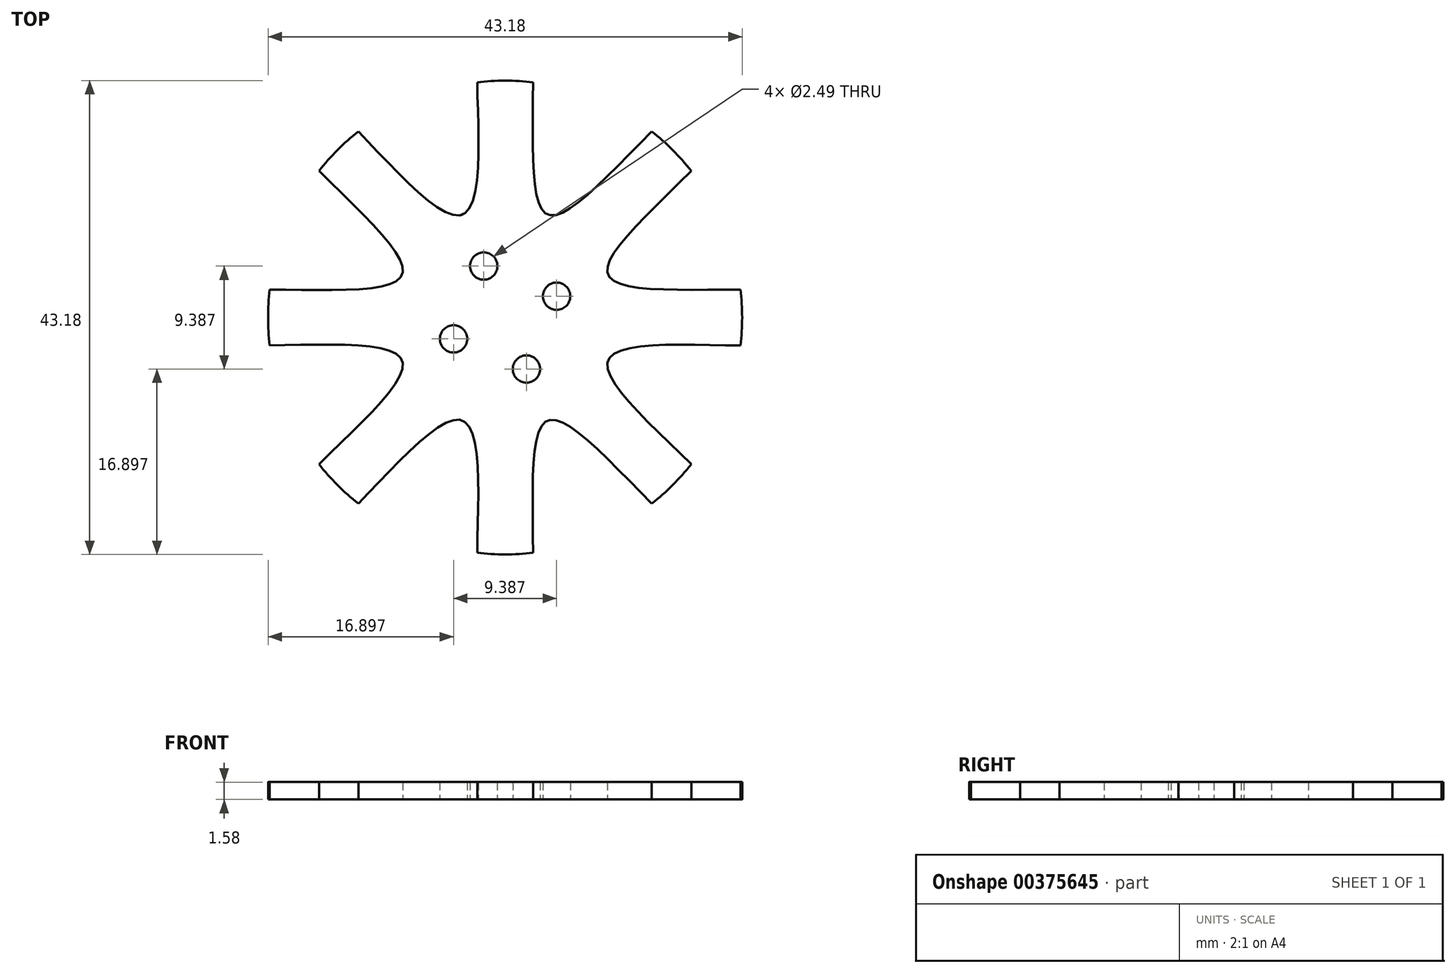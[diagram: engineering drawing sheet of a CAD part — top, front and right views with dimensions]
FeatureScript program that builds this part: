
annotation { "Feature Type Name" : "Feature", "Feature Type Description" : "" }
export const myFeature = defineFeature(function(context is Context, id is Id, definition is map)
    precondition{}
    {
        {
            var Q0;
            Q0=qCreatedBy(makeId("Top.planeOp"),FACE);
            var sketch = newSketch(context, id + "F0", { "sketchPlane" : qUnion([Q0])});
            skLineSegment(sketch, "E0", {"start": v(0, 30.67) * mm, "end": v(0, -28.01) * mm, "construction": true});
            skLineSegment(sketch, "E1", {"start": v(-28.25, 0) * mm, "end": v(29.1, 0) * mm, "construction": true});
            skLineSegment(sketch, "E2", {"start": v(-21.4, 21.4) * mm, "end": v(20.62, -20.62) * mm, "construction": true});
            skLineSegment(sketch, "E3", {"start": v(21.66, 21.66) * mm, "end": v(-18.96, -18.96) * mm, "construction": true});
            skArc(sketch, "E4", {"start": v(-16.96, 13.36) * mm, "mid": v(-15.27, 15.27) * mm, "end": v(-13.36, 16.96) * mm});
            skArc(sketch, "E5", {"start": v(-2.54, 21.44) * mm, "mid": v(0, 21.59) * mm, "end": v(2.54, 21.44) * mm});
            skArc(sketch, "E6", {"start": v(13.36, 16.96) * mm, "mid": v(15.27, 15.27) * mm, "end": v(16.96, 13.36) * mm});
            skArc(sketch, "E7", {"start": v(-13.36, 16.96) * mm, "mid": v(-6.9, 16.66) * mm, "end": v(-2.54, 21.44) * mm});
            skArc(sketch, "E8", {"start": v(2.54, 21.44) * mm, "mid": v(6.9, 16.66) * mm, "end": v(13.36, 16.96) * mm});
            skArc(sketch, "E9", {"start": v(21.44, 2.54) * mm, "mid": v(21.6, 0) * mm, "end": v(21.44, -2.54) * mm});
            skArc(sketch, "E10", {"start": v(16.96, -13.36) * mm, "mid": v(15.27, -15.27) * mm, "end": v(13.36, -16.96) * mm});
            skArc(sketch, "E11", {"start": v(2.54, -21.44) * mm, "mid": v(0, -21.6) * mm, "end": v(-2.54, -21.44) * mm});
            skArc(sketch, "E12", {"start": v(-13.36, -16.96) * mm, "mid": v(-15.27, -15.27) * mm, "end": v(-16.96, -13.36) * mm});
            skArc(sketch, "E13", {"start": v(-21.44, -2.54) * mm, "mid": v(-21.59, 0) * mm, "end": v(-21.44, 2.54) * mm});
            skArc(sketch, "E14", {"start": v(-21.44, 2.54) * mm, "mid": v(-16.66, 6.9) * mm, "end": v(-16.96, 13.36) * mm});
            skArc(sketch, "E15", {"start": v(-16.96, -13.36) * mm, "mid": v(-16.66, -6.9) * mm, "end": v(-21.44, -2.54) * mm});
            skArc(sketch, "E16", {"start": v(-2.54, -21.44) * mm, "mid": v(-6.9, -16.66) * mm, "end": v(-13.36, -16.96) * mm});
            skArc(sketch, "E17", {"start": v(13.36, -16.96) * mm, "mid": v(6.9, -16.66) * mm, "end": v(2.54, -21.44) * mm});
            skArc(sketch, "E18", {"start": v(21.44, -2.54) * mm, "mid": v(16.66, -6.9) * mm, "end": v(16.96, -13.36) * mm});
            skArc(sketch, "E19", {"start": v(16.96, 13.36) * mm, "mid": v(16.66, 6.9) * mm, "end": v(21.44, 2.54) * mm});
            skCircle(sketch, "E20", {"center": v(0, 0) * mm, "radius": 5.08 * mm, "construction": true});
            skCircle(sketch, "E21", {"center": v(4.7, 1.94) * mm, "radius": 1.24 * mm});
            skCircle(sketch, "E22", {"center": v(-4.7, -1.94) * mm, "radius": 1.24 * mm});
            skCircle(sketch, "E23", {"center": v(1.94, -4.7) * mm, "radius": 1.24 * mm});
            skLineSegment(sketch, "E24", {"start": v(-2.42, 5.85) * mm, "end": v(2.68, -6.46) * mm, "construction": true});
            skLineSegment(sketch, "E25", {"start": v(6.63, 2.74) * mm, "end": v(-6.69, -2.77) * mm, "construction": true});
            skCircle(sketch, "E26", {"center": v(-1.94, 4.7) * mm, "radius": 1.24 * mm});
            skSolve(sketch);
        }
        {
            var Q0;
            Q0 = qSketchRegion(id + "F0", true);
            extrude(context, id + "F1", {"entities" : qUnion([Q0]), "endBound" : BoundingType.SYMMETRIC, "depth" : 1.59 * mm});
        }
        {
            var Q0;
            Q0=qCreatedBy(makeId("Front.planeOp"),FACE);
            var sketch = newSketch(context, id + "F2", { "sketchPlane" : qUnion([Q0])});
            skLineSegment(sketch, "E27", {"start": v(0, 9.03) * mm, "end": v(0, -9.77) * mm, "construction": true});
            skSolve(sketch);
        }
        {
            var Q0;
            Q0=makeQuery(id+"F1.opExtrude","CAP_EDGE",EDGE,{"disambiguationData":[OSD([sQuery(id+"F0.wireOp",EDGE,"E6")])],"isStart":false});
            cPoint(context, id + "F3", {"entities" : qUnion([Q0]), "parameter" : 0.5});
        }
        {
            var Q0;
            Q0=makeQuery(id+"F1.opExtrude","CAP_EDGE",EDGE,{"disambiguationData":[OSD([sQuery(id+"F0.wireOp",EDGE,"E6")])],"isStart":false});
            var Q1;
            Q1 = qCreatedBy(id + "F3" ,VERTEX);
            cPlane(context, id + "F4", {"entities" : qUnion([Q0, Q1]), "cplaneType" : CPlaneType.CURVE_POINT, "offset" : 25.4 * mm, "width" : 152.4 * mm, "height" : 152.4 * mm});
        }
        {
            var Q0;
            Q0=makeQuery(id+"F1.opExtrude","CAP_FACE",FACE,{"disambiguationData":[OSD([sQuery(id+"F0.wireOp",EDGE,"E4"),sQuery(id+"F0.wireOp",EDGE,"E5"),sQuery(id+"F0.wireOp",EDGE,"E6"),sQuery(id+"F0.wireOp",EDGE,"E7"),sQuery(id+"F0.wireOp",EDGE,"E8"),sQuery(id+"F0.wireOp",EDGE,"E9"),sQuery(id+"F0.wireOp",EDGE,"E10"),sQuery(id+"F0.wireOp",EDGE,"E11"),sQuery(id+"F0.wireOp",EDGE,"E12"),sQuery(id+"F0.wireOp",EDGE,"E13"),sQuery(id+"F0.wireOp",EDGE,"E14"),sQuery(id+"F0.wireOp",EDGE,"E15"),sQuery(id+"F0.wireOp",EDGE,"E16"),sQuery(id+"F0.wireOp",EDGE,"E17"),sQuery(id+"F0.wireOp",EDGE,"E18"),sQuery(id+"F0.wireOp",EDGE,"E19"),sQuery(id+"F0.wireOp",EDGE,"E21"),sQuery(id+"F0.wireOp",EDGE,"E22"),sQuery(id+"F0.wireOp",EDGE,"E23"),sQuery(id+"F0.wireOp",EDGE,"E26")])],"isStart":false});
            var sketch = newSketch(context, id + "F5", { "sketchPlane" : qUnion([Q0])});
            skLineSegment(sketch, "E28", {"start": v(-19.28, -7.99) * mm, "end": v(21.9, 9.07) * mm, "construction": true});
            skFitSpline(sketch, "E29", {"points": [v(16.96, 13.36) * mm, v(9.39, 3.89) * mm, v(21.44, 2.54) * mm], "startDerivative": vector(-25.12, -25.19) * mm, "endDerivative": vector(34.63, -0.1) * mm});
            skLineSegment(sketch, "E30", {"start": v(-9.53, 23.02) * mm, "end": v(9.33, -22.54) * mm, "construction": true});
            skFitSpline(sketch, "E31", {"points": [v(2.54, -21.44) * mm, v(3.89, -9.39) * mm, v(13.36, -16.96) * mm], "startDerivative": vector(-0.02, 34.1) * mm, "endDerivative": vector(24.11, -24.05) * mm});
            skLineSegment(sketch, "E32", {"start": v(-21.4, 8.86) * mm, "end": v(22.41, -9.28) * mm, "construction": true});
            skLineSegment(sketch, "E33", {"start": v(8.34, 20.12) * mm, "end": v(-8.56, -20.68) * mm, "construction": true});
            skFitSpline(sketch, "E34", {"points": [v(21.44, -2.54) * mm, v(9.39, -3.89) * mm, v(16.96, -13.36) * mm], "startDerivative": vector(-31.53, 0.26) * mm, "endDerivative": vector(22.55, -22.16) * mm});
            skFitSpline(sketch, "E35", {"points": [v(-13.36, -16.96) * mm, v(-3.89, -9.39) * mm, v(-2.54, -21.44) * mm], "startDerivative": vector(20.74, 21.37) * mm, "endDerivative": vector(-0.44, -29.69) * mm});
            skFitSpline(sketch, "E36", {"points": [v(-21.44, -2.54) * mm, v(-9.39, -3.89) * mm, v(-16.96, -13.36) * mm], "startDerivative": vector(32, 0.4) * mm, "endDerivative": vector(-22.71, -22.36) * mm});
            skFitSpline(sketch, "E37", {"points": [v(-16.96, 13.36) * mm, v(-9.39, 3.89) * mm, v(-21.44, 2.54) * mm], "startDerivative": vector(23.96, -23.72) * mm, "endDerivative": vector(-33.75, 0.07) * mm});
            skFitSpline(sketch, "E38", {"points": [v(-13.36, 16.96) * mm, v(-3.89, 9.39) * mm, v(-2.54, 21.44) * mm], "startDerivative": vector(19.49, -20.2) * mm, "endDerivative": vector(-0.54, 28.11) * mm});
            skFitSpline(sketch, "E39", {"points": [v(2.54, 21.44) * mm, v(3.89, 9.39) * mm, v(13.36, 16.96) * mm], "startDerivative": vector(0.05, -34.8) * mm, "endDerivative": vector(24.68, 24.63) * mm});
            skSolve(sketch);
        }
        {
            var Q0;
            Q0=makeQuery(id+"F5.imprint","IMPRINT",FACE,{"disambiguationData":[TD([[makeQuery(id+"F5.imprint","IMPRINT",EDGE,{"derivedFrom":sQuery(id+"F5.wireOp",EDGE,"E29")}),1.0]])]});
            var Q1;
            Q1=makeQuery(id+"F5.imprint","IMPRINT",FACE,{"disambiguationData":[TD([[makeQuery(id+"F5.imprint","IMPRINT",EDGE,{"derivedFrom":sQuery(id+"F5.wireOp",EDGE,"E31")}),-1.0]])]});
            var Q2;
            Q2=makeQuery(id+"F5.imprint","IMPRINT",FACE,{"disambiguationData":[TD([[makeQuery(id+"F5.imprint","IMPRINT",EDGE,{"derivedFrom":sQuery(id+"F5.wireOp",EDGE,"E34")}),1.0]])]});
            var Q3;
            Q3=makeQuery(id+"F5.imprint","IMPRINT",FACE,{"disambiguationData":[TD([[makeQuery(id+"F5.imprint","IMPRINT",EDGE,{"derivedFrom":sQuery(id+"F5.wireOp",EDGE,"E35")}),-1.0]])]});
            var Q4;
            Q4=makeQuery(id+"F5.imprint","IMPRINT",FACE,{"disambiguationData":[TD([[makeQuery(id+"F5.imprint","IMPRINT",EDGE,{"derivedFrom":sQuery(id+"F5.wireOp",EDGE,"E39")}),1.0]])]});
            var Q5;
            Q5=makeQuery(id+"F5.imprint","IMPRINT",FACE,{"disambiguationData":[TD([[makeQuery(id+"F5.imprint","IMPRINT",EDGE,{"derivedFrom":sQuery(id+"F5.wireOp",EDGE,"E38")}),1.0]])]});
            var Q6;
            Q6=makeQuery(id+"F5.imprint","IMPRINT",FACE,{"disambiguationData":[TD([[makeQuery(id+"F5.imprint","IMPRINT",EDGE,{"derivedFrom":sQuery(id+"F5.wireOp",EDGE,"E37")}),-1.0]])]});
            var Q7;
            Q7=makeQuery(id+"F5.imprint","IMPRINT",FACE,{"disambiguationData":[TD([[makeQuery(id+"F5.imprint","IMPRINT",EDGE,{"derivedFrom":sQuery(id+"F5.wireOp",EDGE,"E36")}),-1.0]])]});
            extrude(context, id + "F6", {"entities" : qUnion([Q0, Q1, Q2, Q3, Q4, Q5, Q6, Q7]), "operationType" : NewBodyOperationType.REMOVE, "endBound" : BoundingType.UP_TO_NEXT, "oppositeDirection" : true, "depth" : 25.4 * mm, "offsetDistance" : 25.4 * mm});
        }
    });
